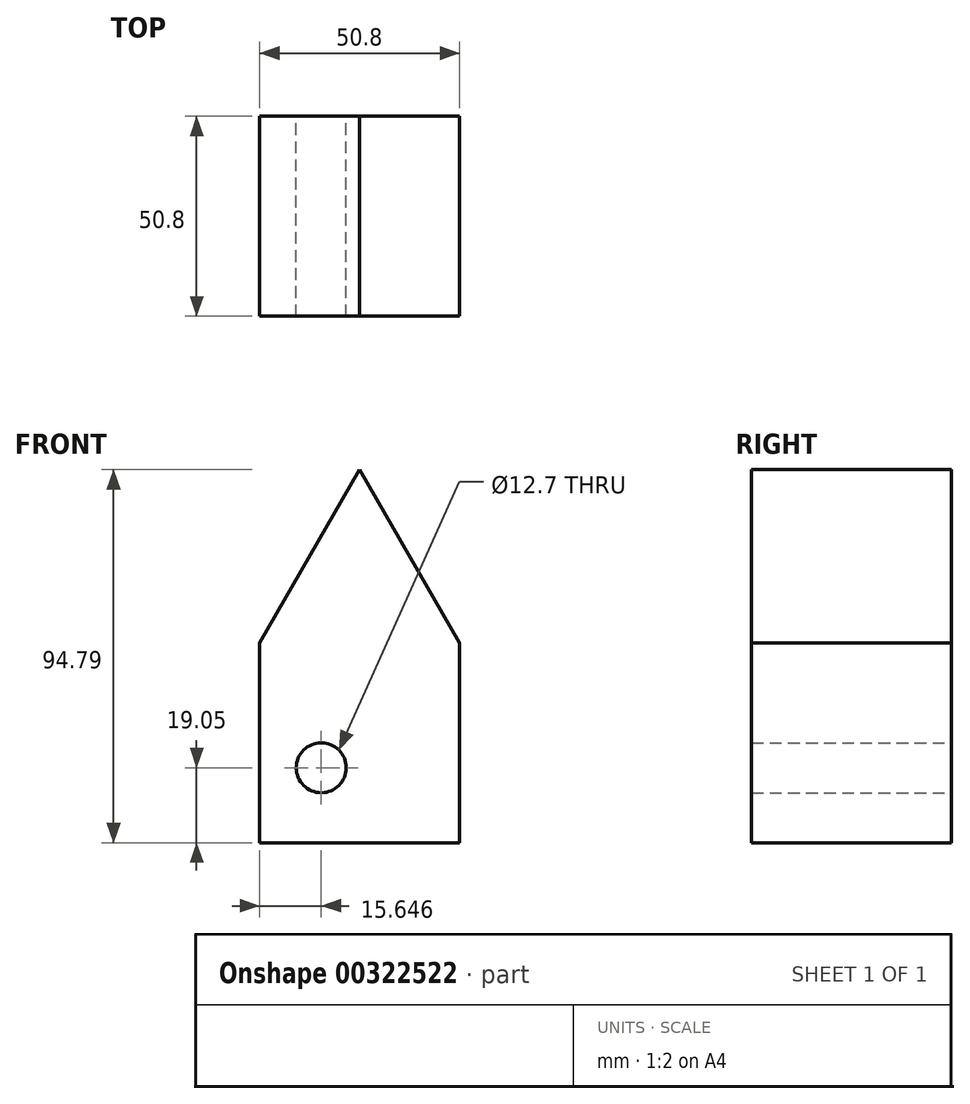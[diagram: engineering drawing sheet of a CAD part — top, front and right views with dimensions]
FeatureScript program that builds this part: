
annotation { "Feature Type Name" : "Feature", "Feature Type Description" : "" }
export const myFeature = defineFeature(function(context is Context, id is Id, definition is map)
    precondition{}
    {
        {
            var Q0;
            Q0=qCreatedBy(makeId("Front.planeOp"),FACE);
            var sketch = newSketch(context, id + "F0", { "sketchPlane" : qUnion([Q0])});
            skLineSegment(sketch, "E0.bottom", {"start": v(25.4, -19.05) * mm, "end": v(-25.4, -19.05) * mm});
            skLineSegment(sketch, "E0.left", {"start": v(25.4, -19.05) * mm, "end": v(25.4, 31.75) * mm});
            skLineSegment(sketch, "E0.right", {"start": v(-25.4, -19.05) * mm, "end": v(-25.4, 31.75) * mm});
            skPoint(sketch, "E0.middle", {"position": v(0, 6.35) * mm});
            skPoint(sketch, "E1.middle", {"position": v(0, -19.05) * mm});
            skPoint(sketch, "E1.cornerSnap0", {"position": v(0, -19.05) * mm});
            skLineSegment(sketch, "E2", {"start": v(-25.4, 31.75) * mm, "end": v(0, 75.74) * mm});
            skLineSegment(sketch, "E3", {"start": v(25.4, 31.75) * mm, "end": v(0, 75.74) * mm});
            skCircle(sketch, "E4", {"center": v(-9.75, 0) * mm, "radius": 6.35 * mm});
            skSolve(sketch);
        }
        {
            var Q0;
            Q0=makeQuery(id+"F0.imprint","IMPRINT",FACE,{"disambiguationData":[TD([[makeQuery(id+"F0.imprint","IMPRINT",EDGE,{"derivedFrom":sQuery(id+"F0.wireOp",EDGE,"E0.bottom")}),-1.0]])]});
            extrude(context, id + "F1", {"entities" : qUnion([Q0]), "depth" : 50.8 * mm});
        }
    });
